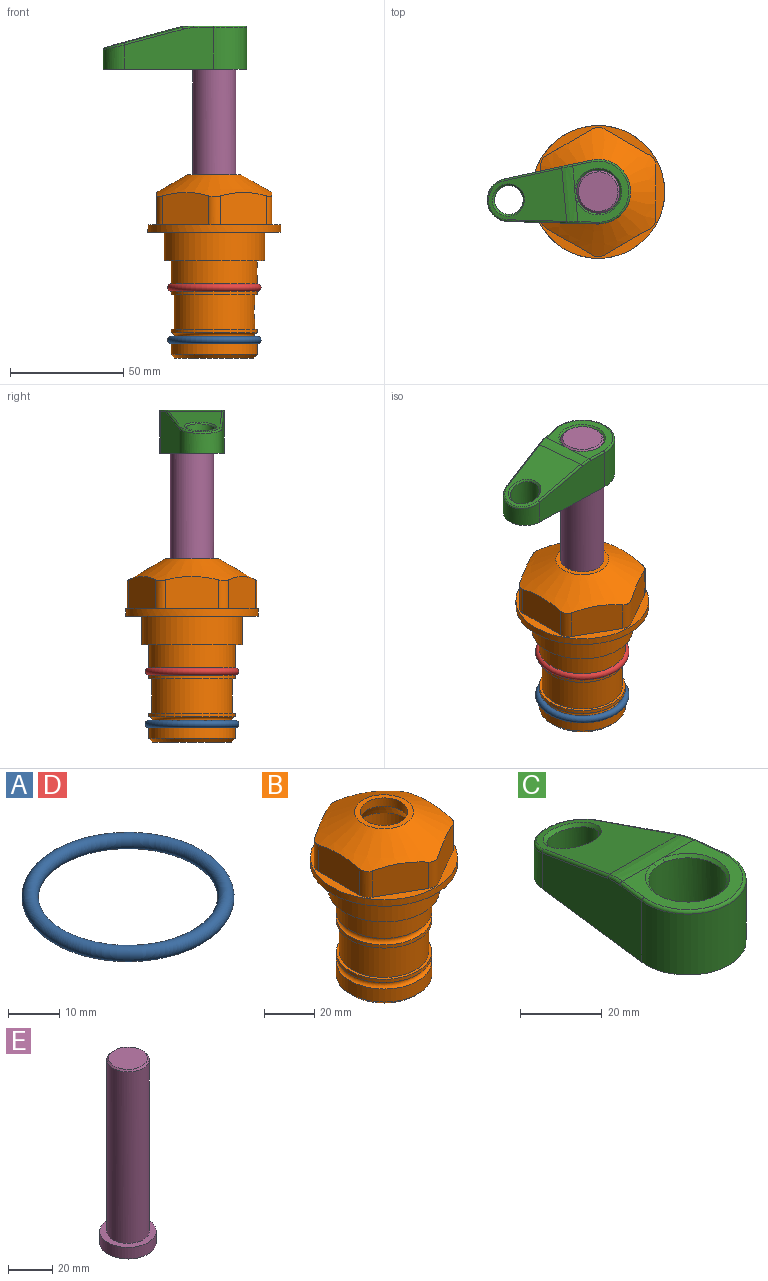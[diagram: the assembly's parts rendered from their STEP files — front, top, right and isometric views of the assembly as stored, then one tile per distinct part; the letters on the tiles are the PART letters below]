
ASSEMBLY  parts=5 mates=3
PART A: 1 faces, bbox 44.7x44.7x3.2 mm
  f0: torus R=19.05mm, axis (0,0,1), area 1193.9mm2
PART B: 36 faces, bbox 58.7x58.7x81 mm
  f0: cylinder r=17.78mm len=35.56mm, axis (0,0,1), area 1670.8mm2, adj f23,f24,f31
  f1: cylinder r=19.05mm len=38.1mm, axis (0,0,1), area 1191.9mm2, adj f26,f27,f30
  f2: plane 58.66x58.66mm, normal (0,0,-1), area 1150.6mm2, adj f3,f28
  f3: cylinder r=29.33mm len=58.66mm, axis (0,0,-1), area 585.1mm2, adj f2,f4
  f4: plane 58.66x58.66mm, normal (0,0,1), area 475.9mm2, adj f3,f5,f6,f7,f8,f9,f10,f11
  f5: plane 20.32x14.34mm, normal (-0.5,0.87,0), area 324.4mm2, adj f4,f15,f16,f17
  f6: plane 20.32x14.34mm, normal (0.5,0.87,0), area 324.4mm2, adj f4,f14,f15,f17
  f7: plane 23.48x14.34mm, normal (1,0,0), area 324.4mm2, adj f4,f13,f14,f17
  f8: plane 20.32x14.34mm, normal (0.5,-0.87,0), area 324.4mm2, adj f4,f12,f13,f17
  f9: plane 20.32x14.34mm, normal (-0.5,-0.87,0), area 324.4mm2, adj f4,f11,f12,f17
  f10: plane 23.48x14.34mm, normal (-1,0,0), area 324.4mm2, adj f4,f11,f16,f17
  f11: cylinder r=5.08mm len=12.85mm, axis (0,0,-1), area 67.2mm2, adj f4,f9,f10,f17
  f12: cylinder r=5.08mm len=12.85mm, axis (0,0,-1), area 67.2mm2, adj f4,f8,f9,f17
  f13: cylinder r=5.08mm len=12.85mm, axis (0,0,-1), area 67.2mm2, adj f4,f7,f8,f17
  f14: cylinder r=5.08mm len=12.85mm, axis (0,0,-1), area 67.2mm2, adj f4,f6,f7,f17
  f15: cylinder r=5.08mm len=12.85mm, axis (0,0,-1), area 67.2mm2, adj f4,f5,f6,f17
  f16: cylinder r=5.08mm len=12.85mm, axis (0,0,-1), area 67.2mm2, adj f4,f5,f10,f17
  f17: cone r=11.73mm half-angle=60deg, axis (0,0,-1), area 2071.8mm2, adj f5,f6,f7,f8,f9,f10,f11,f12
  f18: plane 23.46x23.46mm, normal (0,0,1), area 147.4mm2, adj f17,f35
  f19: plane 34.93x34.93mm, normal (0,0,-1), area 958mm2, adj f29
  f20: cylinder r=19.05mm len=38.1mm, axis (0,0,1), area 760.1mm2, adj f21,f29
  f21: torus R=19.05mm, axis (0,0,1), area 565.3mm2, adj f20,f22
  f22: cylinder r=19.05mm len=38.1mm, axis (0,0,1), area 190mm2, adj f21,f23
  f23: plane 38.1x38.1mm, normal (0,0,1), area 146.9mm2, adj f0,f22
  f24: plane 38.1x38.1mm, normal (0,0,-1), area 146.9mm2, adj f0,f25
  f25: cylinder r=19.05mm len=38.1mm, axis (0,0,1), area 190mm2, adj f24,f26
  f26: torus R=19.05mm, axis (0,0,1), area 565.3mm2, adj f1,f25
  f27: plane 44.45x44.45mm, normal (0,0,-1), area 411.7mm2, adj f1,f28
  f28: cylinder r=22.23mm len=44.45mm, axis (0,0,1), area 1773.5mm2, adj f2,f27
  f29: cone r=19.05mm half-angle=45deg, axis (0,0,1), area 257.5mm2, adj f19,f20
  f30: cylinder r=3.17mm len=6.75mm, axis (-1,0,0), area 128mm2, adj f1,f33
  f31: cylinder r=3.17mm len=6.35mm, axis (-1,0,0), area 102.5mm2, adj f0,f33
  f32: plane 25.4x25.4mm, normal (0,0,1), area 506.7mm2, adj f33
  f33: cylinder r=12.7mm len=66.42mm, axis (0,0,-1), area 5236.2mm2, adj f30,f31,f32,f34
  f34: cone r=9.53mm half-angle=30deg, axis (0,0,-1), area 443.4mm2, adj f33,f35
  f35: cylinder r=9.53mm len=19.05mm, axis (0,0,-1), area 240.9mm2, adj f18,f34
PART C: 31 faces, bbox 31.7x65.5x19.8 mm
  f0: plane 39.12x18.26mm, normal (0.99,0.12,0), area 612.2mm2, adj f1,f4,f7,f11,f13,f15
  f1: cylinder r=9.53mm len=18.91mm, axis (0,0,-1), area 296.1mm2, adj f0,f2,f7,f17
  f2: plane 39.12x18.26mm, normal (-0.99,0.12,0), area 612.2mm2, adj f1,f4,f7,f12,f14,f16
  f3: cylinder r=6.35mm len=12.7mm, axis (0,0,-1), area 362.4mm2, adj f7,f18
  f4: cylinder r=14.29mm len=28.58mm, axis (0,0,-1), area 882.2mm2, adj f0,f2,f7,f10
  f5: cylinder r=9.53mm len=19.05mm, axis (0,0,-1), area 1092.6mm2, adj f7,f19,f20
  f6: plane 26.99x23.69mm, normal (0,0,1), area 216.2mm2, adj f9,f10,f11,f12,f19
  f7: plane 63.5x28.58mm, normal (0,0,-1), area 661.8mm2, adj f0,f1,f2,f3,f4,f5,f22,f23
  f8: plane 33.52x23.6mm, normal (0,0.26,0.97), area 486mm2, adj f9,f15,f16,f17,f18
  f9: cylinder r=19.05mm len=24.72mm, axis (1,0,0), area 120.4mm2, adj f6,f8,f13,f14,f20
  f10: torus R=13.49mm, axis (0,0,1), area 59mm2, adj f4,f6,f11,f12
  f11: cylinder r=0.79mm len=8.67mm, axis (0.12,-0.99,0), area 10.8mm2, adj f0,f6,f10,f13
  f12: cylinder r=0.79mm len=8.67mm, axis (0.12,0.99,0), area 10.8mm2, adj f2,f6,f10,f14
  f13: bspline ~4.95x1.42mm, area 6.1mm2, adj f0,f9,f11,f15
  f14: bspline ~4.95x1.42mm, area 6.1mm2, adj f2,f9,f12,f16
  f15: cylinder r=0.79mm len=25.95mm, axis (0.12,-0.96,0.26), area 32.9mm2, adj f0,f8,f13,f17
  f16: cylinder r=0.79mm len=25.95mm, axis (0.12,0.96,-0.26), area 32.9mm2, adj f2,f8,f14,f17
  f17: bspline ~18.91x8.38mm, area 30mm2, adj f1,f8,f15,f16
  f18: bspline ~14.29x14.29mm, area 48.3mm2, adj f3,f8
  f19: cone r=9.53mm half-angle=45deg, axis (0,0,1), area 66.5mm2, adj f5,f6,f20
  f20: bspline ~3.22x0.96mm, area 3.5mm2, adj f5,f9,f19
  f21: plane 2.75x2.72mm, normal (0,0,-1), area 2.9mm2, adj f23,f25,f28
  f22: plane 23.05x15.88mm, normal (-0.99,-0.12,0), area 323.6mm2, adj f7,f25,f26,f27,f28,f29
  f23: plane 23.05x15.88mm, normal (0.99,-0.12,0), area 323.6mm2, adj f7,f21,f25,f27,f28,f30
  f24: cylinder r=9.53mm len=10.69mm, axis (0,0,-1), area 114.7mm2, adj f7,f27,f29,f30
  f25: cylinder r=12.7mm len=20.59mm, axis (0,0,-1), area 381.1mm2, adj f7,f21,f22,f23,f26,f28
  f26: plane 2.75x2.72mm, normal (0,0,-1), area 2.9mm2, adj f22,f25,f28
  f27: plane 19.72x18.37mm, normal (0,-0.26,-0.97), area 291.8mm2, adj f22,f23,f24,f28,f29,f30
  f28: cylinder r=15.88mm len=19.92mm, axis (1,0,0), area 54.8mm2, adj f21,f22,f23,f25,f26,f27
  f29: cylinder r=1.59mm len=11mm, axis (0,0,-1), area 34.7mm2, adj f7,f22,f24,f27
  f30: cylinder r=1.59mm len=11mm, axis (0,0,-1), area 34.7mm2, adj f7,f23,f24,f27
PART D: same geometry as A
PART E: 6 faces, bbox 25.4x25.4x101.6 mm
  f0: plane 17.46x17.46mm, normal (0,0,1), area 239.5mm2, adj f5
  f1: plane 25.4x25.4mm, normal (0,0,-1), area 506.7mm2, adj f2
  f2: cylinder r=12.7mm len=25.4mm, axis (0,0,1), area 506.7mm2, adj f1,f3
  f3: plane 25.4x25.4mm, normal (0,0,1), area 221.7mm2, adj f2,f4
  f4: cylinder r=9.53mm len=94.46mm, axis (0,0,1), area 5653mm2, adj f3,f5
  f5: cone r=8.73mm half-angle=45deg, axis (0,0,-1), area 64.4mm2, adj f0,f4
PLACE A t=(0,0,-23.18)mm
PLACE B at identity fixed
PLACE C rot(axis=(0,0,1),95.3deg) t=(0,0,27.55)mm
PLACE D at identity
PLACE E rot(axis=(0,0,1),95.3deg) t=(0,0,27.55)mm
MATE fastened E.f2 <-> C.f4  axis (0,0,1) through (0,0,91.05)mm
MATE cylindrical B.f0 <-> E.f2  axis (0,0,1) through (0,0,-50.55)mm
MATE fastened A.f0 <-> B.f0  axis (0,0,1) through (0,0,-47.69)mm
